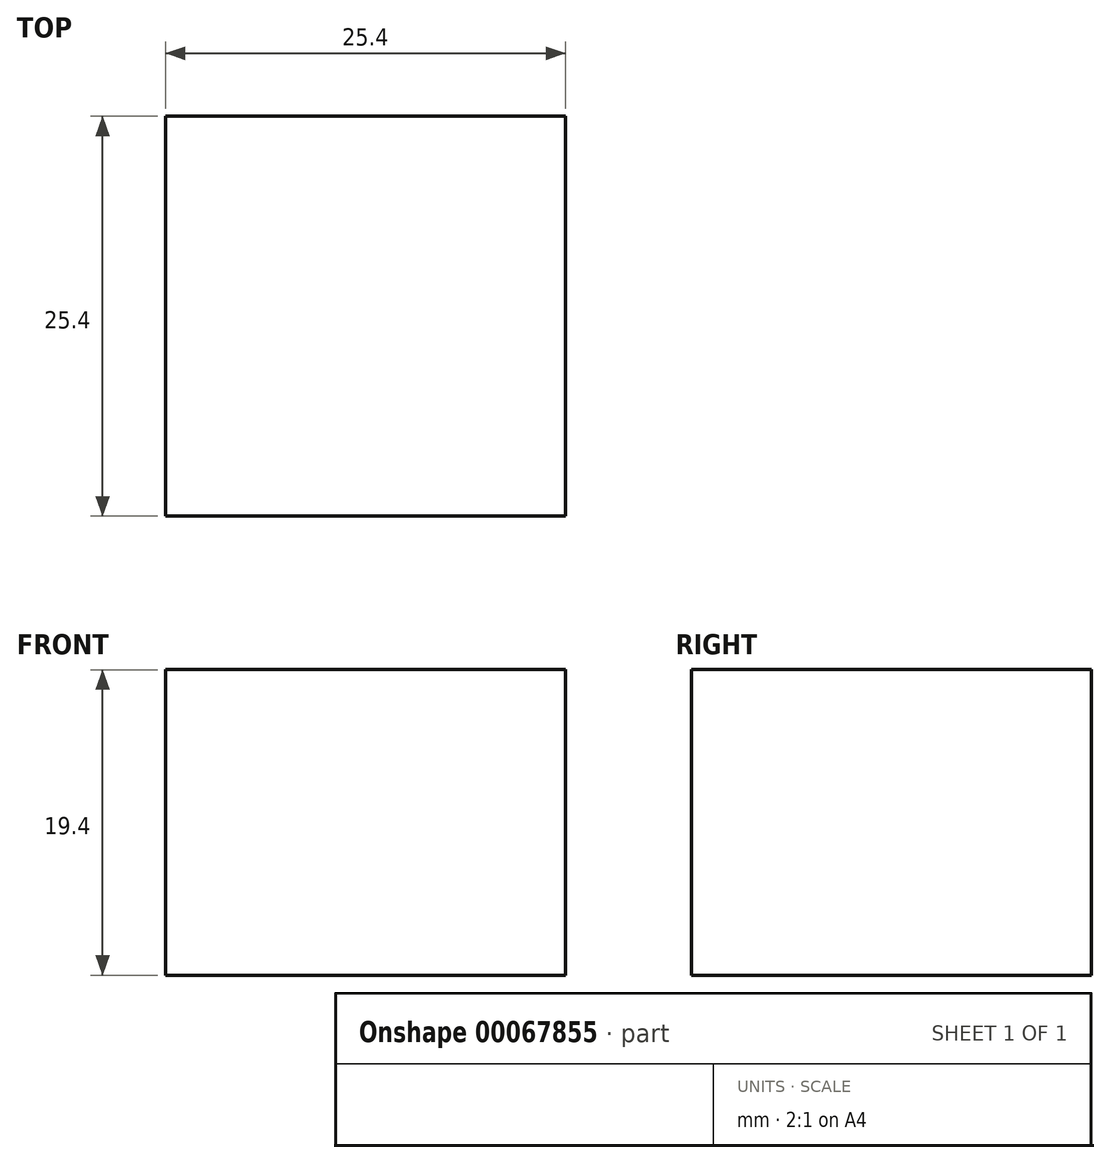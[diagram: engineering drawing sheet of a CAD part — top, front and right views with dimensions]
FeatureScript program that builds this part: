
annotation { "Feature Type Name" : "Feature", "Feature Type Description" : "" }
export const myFeature = defineFeature(function(context is Context, id is Id, definition is map)
    precondition{}
    {
        {
            var Q0;
            Q0=qCreatedBy(makeId("Front.planeOp"),FACE);
            var sketch = newSketch(context, id + "F0", { "sketchPlane" : qUnion([Q0])});
            skLineSegment(sketch, "E0.bottom", {"start": v(0, 0) * mm, "end": v(25.4, 0) * mm});
            skLineSegment(sketch, "E0.top", {"start": v(0, 19.4) * mm, "end": v(25.4, 19.4) * mm});
            skLineSegment(sketch, "E0.left", {"start": v(0, 0) * mm, "end": v(0, 19.4) * mm});
            skLineSegment(sketch, "E0.right", {"start": v(25.4, 0) * mm, "end": v(25.4, 19.4) * mm});
            skSolve(sketch);
        }
        {
            var Q0;
            Q0=makeQuery(id+"F0.imprint","IMPRINT",FACE,{"disambiguationData":[TD([[makeQuery(id+"F0.imprint","IMPRINT",EDGE,{"derivedFrom":sQuery(id+"F0.wireOp",EDGE,"E0.bottom")}),1.0]])]});
            extrude(context, id + "F1", {"entities" : qUnion([Q0]), "depth" : 25.4 * mm});
        }
    });
